# Revit family: io Pendant 1000
name_source: partatom
category: Lighting Fixtures
units: mm (PartAtom-declared; Revit-internal decimal feet)

## family parameters
Always vertical = Yes
Cut with Voids When Loaded = No
Host = Ceiling
Light Source = Yes
OmniClass Number = 23.80.70.11
OmniClass Title = Luminaries for Internal Lighting
Part Type = Normal
Room Calculation Point = No
Round Connector Dimension = Use Diameter
Shared = No

## types (1)
- UL
    ADA compliant = Yes - if installed in compliance with ADA §307.4
    Color Filter = 16777215
    Default Elevation = 0 mm  [stored 0 ft]
    Dimmable = Yes
    Dimming Lamp Color Temperature Shift = <None>
    Dimming Method = Phase - Leading & Trailing Edge
    Driver Included = Yes (integral)
    Driver Required = No
    Efficacy (lm/w) = 104
    Electrical Class = 1
    Lamp = LED
    Length of supplied cable = 78.74in
    Light Source Fixed = Yes
    Location / IP Rating = DRY
    Main Finish = Clear
    Main Material = Glass
    Manufacturer URL - Europe and Rest of World = www.astrolighting.com
    Manufacturer URL - North America = us.astrolighting.com
    Max Drop (pendants) = 83.19in
    Photometric Web File = 1409016_io Pendant 1000 UL_Photometry_IES_Iss.01.ies
    Power (Watts) = 21
    Product CCT = 3000K
    Product CRI = 80
    Product Dimensions (MM) = see datasheet
    Product Location = Indoor
    Product Name = io Pendant 1000
    Product SKU = 1409016
    Product Weight (KG) = 3 mm  [stored 0.00984252 ft]
    Tilt Angle = 0.00°

note: [stored X ft] marks values corroborated as IEEE doubles in the binary element streams (Revit-internal decimal feet)

## geometry (parser evidence)
native form markers: Sweep x3
no freeform markers — native parametric forms only
